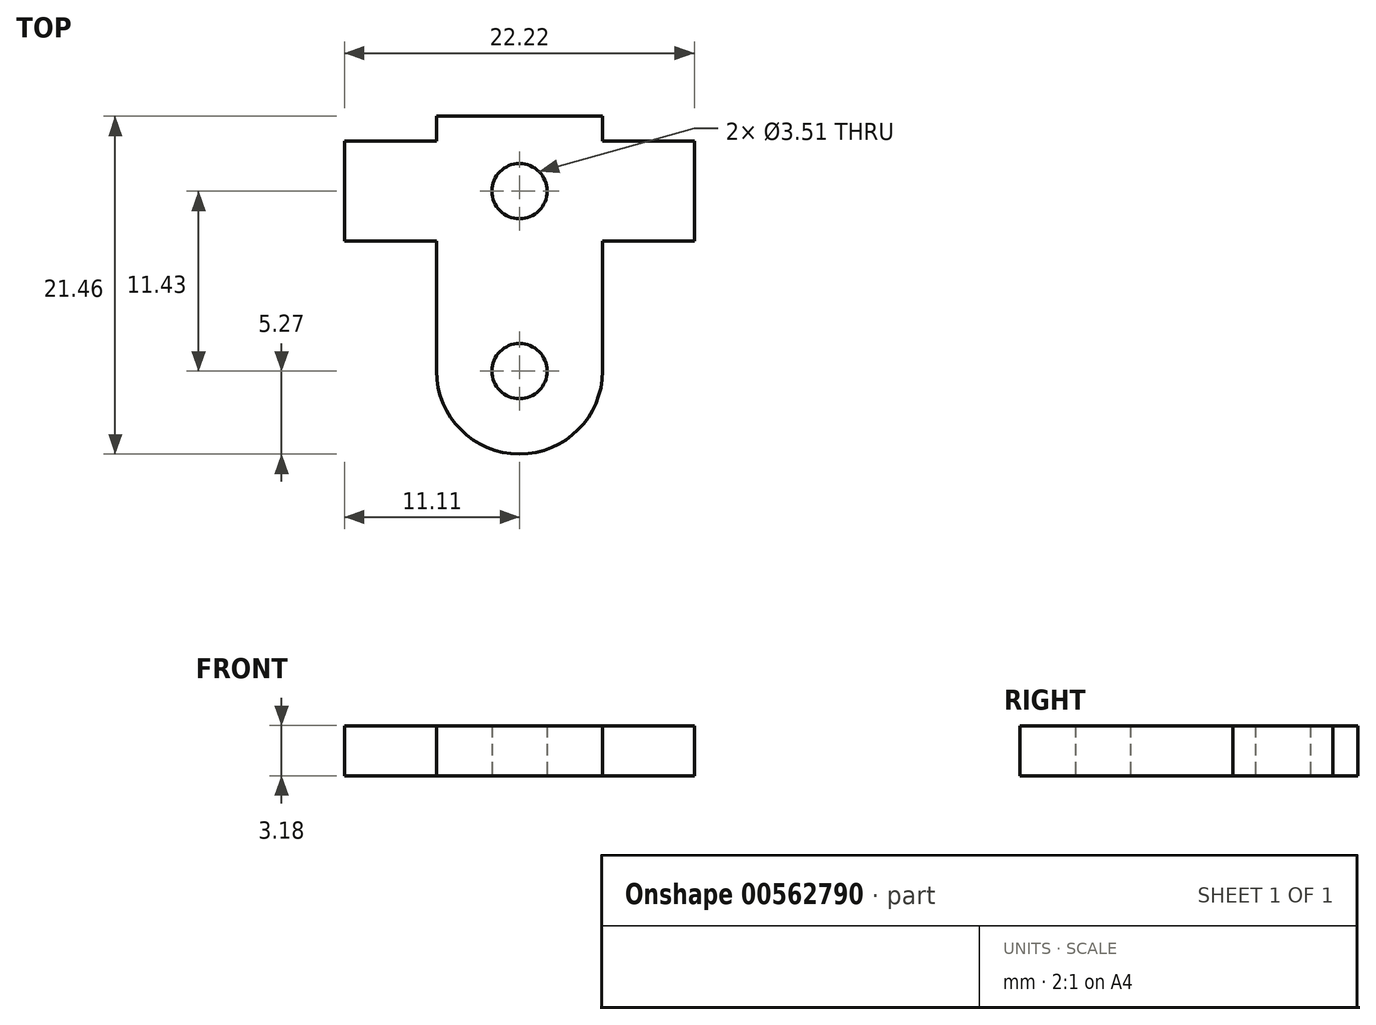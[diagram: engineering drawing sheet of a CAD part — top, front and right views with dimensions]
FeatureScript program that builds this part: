
annotation { "Feature Type Name" : "Feature", "Feature Type Description" : "" }
export const myFeature = defineFeature(function(context is Context, id is Id, definition is map)
    precondition{}
    {
        {
            var Q0;
            Q0=qCreatedBy(makeId("Top.planeOp"),FACE);
            var sketch = newSketch(context, id + "F0", { "sketchPlane" : qUnion([Q0])});
            skLineSegment(sketch, "E0.bottom", {"start": v(-11.11, 3.17) * mm, "end": v(-5.27, 3.17) * mm});
            skLineSegment(sketch, "E0.top", {"start": v(-11.11, -3.18) * mm, "end": v(-5.27, -3.18) * mm});
            skLineSegment(sketch, "E0.left", {"start": v(-11.11, 3.17) * mm, "end": v(-11.11, -3.18) * mm});
            skLineSegment(sketch, "E0.right", {"start": v(11.11, 3.17) * mm, "end": v(11.11, -3.18) * mm});
            skPoint(sketch, "E0.middle", {"position": v(0, 0) * mm});
            skLineSegment(sketch, "E1.top", {"start": v(-5.27, 4.76) * mm, "end": v(5.27, 4.76) * mm});
            skLineSegment(sketch, "E1.left", {"start": v(-5.27, 3.17) * mm, "end": v(-5.27, 4.76) * mm});
            skLineSegment(sketch, "E1.right", {"start": v(5.27, 3.17) * mm, "end": v(5.27, 4.76) * mm});
            skPoint(sketch, "E1.middle", {"position": v(0, 3.97) * mm});
            skLineSegment(sketch, "E2.trimOffspring", {"start": v(5.27, 3.17) * mm, "end": v(11.11, 3.17) * mm});
            skLineSegment(sketch, "E3.MirrorCS", {"start": v(5.27, -3.17) * mm, "end": v(5.27, -4.76) * mm});
            skLineSegment(sketch, "E4.MirrorCS", {"start": v(-5.27, -3.17) * mm, "end": v(-5.27, -4.76) * mm});
            skPoint(sketch, "E5.MirrorP", {"position": v(0, -3.97) * mm});
            skLineSegment(sketch, "E6.MirrorCS", {"start": v(-5.27, -4.76) * mm, "end": v(5.27, -4.76) * mm});
            skLineSegment(sketch, "E7.trimOffspring", {"start": v(5.27, -3.18) * mm, "end": v(11.11, -3.18) * mm});
            skSolve(sketch);
        }
        {
            var Q0;
            Q0 = qSketchRegion(id + "F0", true);
            extrude(context, id + "F1", {"entities" : qUnion([Q0]), "depth" : 3.17 * mm, "offsetDistance" : 25.4 * mm});
        }
        {
            var Q0;
            Q0=makeQuery(id+"F1.opExtrude","CAP_FACE",FACE,{"disambiguationData":[OSD([sQuery(id+"F0.wireOp",EDGE,"E0.bottom"),sQuery(id+"F0.wireOp",EDGE,"E0.top"),sQuery(id+"F0.wireOp",EDGE,"E0.left"),sQuery(id+"F0.wireOp",EDGE,"E0.right"),sQuery(id+"F0.wireOp",EDGE,"E1.top"),sQuery(id+"F0.wireOp",EDGE,"E1.left"),sQuery(id+"F0.wireOp",EDGE,"E1.right"),sQuery(id+"F0.wireOp",EDGE,"E2.trimOffspring"),sQuery(id+"F0.wireOp",EDGE,"E3.MirrorCS"),sQuery(id+"F0.wireOp",EDGE,"E4.MirrorCS"),sQuery(id+"F0.wireOp",EDGE,"E6.MirrorCS"),sQuery(id+"F0.wireOp",EDGE,"E7.trimOffspring")])],"isStart":true});
            var sketch = newSketch(context, id + "F2", { "sketchPlane" : qUnion([Q0])});
            skCircle(sketch, "E8", {"center": v(0, 11.43) * mm, "radius": 1.75 * mm});
            skArc(sketch, "E9", {"start": v(5.27, 11.43) * mm, "mid": v(0, 16.7) * mm, "end": v(-5.27, 11.43) * mm});
            skLineSegment(sketch, "E10", {"start": v(-5.27, 4.76) * mm, "end": v(-5.27, 11.43) * mm});
            skLineSegment(sketch, "E11", {"start": v(-5.27, 4.76) * mm, "end": v(5.27, 4.76) * mm});
            skLineSegment(sketch, "E12.MirrorCS", {"start": v(5.27, 4.76) * mm, "end": v(5.27, 11.43) * mm});
            skSolve(sketch);
        }
        {
            var Q0;
            Q0 = qSketchRegion(id + "F2", true);
            var Q1;
            Q1=makeQuery(id+"F1.opExtrude","CAP_FACE",FACE,{"disambiguationData":[OSD([sQuery(id+"F0.wireOp",EDGE,"E0.bottom"),sQuery(id+"F0.wireOp",EDGE,"E0.top"),sQuery(id+"F0.wireOp",EDGE,"E0.left"),sQuery(id+"F0.wireOp",EDGE,"E0.right"),sQuery(id+"F0.wireOp",EDGE,"E1.top"),sQuery(id+"F0.wireOp",EDGE,"E1.left"),sQuery(id+"F0.wireOp",EDGE,"E1.right"),sQuery(id+"F0.wireOp",EDGE,"E2.trimOffspring"),sQuery(id+"F0.wireOp",EDGE,"E3.MirrorCS"),sQuery(id+"F0.wireOp",EDGE,"E4.MirrorCS"),sQuery(id+"F0.wireOp",EDGE,"E6.MirrorCS"),sQuery(id+"F0.wireOp",EDGE,"E7.trimOffspring")])],"isStart":false});
            extrude(context, id + "F3", {"entities" : qUnion([Q0]), "operationType" : NewBodyOperationType.ADD, "endBound" : BoundingType.UP_TO_SURFACE, "oppositeDirection" : true, "depth" : 25.4 * mm, "endBoundEntityFace" : qUnion([Q1]), "offsetDistance" : 25.4 * mm});
        }
        {
            var Q0;
            Q0=makeQuery(id+"F3.boolean.opBoolean","MERGE",FACE,{"derivedFrom":[makeQuery(id+"F1.opExtrude","CAP_FACE",FACE,{"disambiguationData":[OSD([sQuery(id+"F0.wireOp",EDGE,"E0.bottom"),sQuery(id+"F0.wireOp",EDGE,"E0.top"),sQuery(id+"F0.wireOp",EDGE,"E0.left"),sQuery(id+"F0.wireOp",EDGE,"E0.right"),sQuery(id+"F0.wireOp",EDGE,"E1.top"),sQuery(id+"F0.wireOp",EDGE,"E1.left"),sQuery(id+"F0.wireOp",EDGE,"E1.right"),sQuery(id+"F0.wireOp",EDGE,"E2.trimOffspring"),sQuery(id+"F0.wireOp",EDGE,"E3.MirrorCS"),sQuery(id+"F0.wireOp",EDGE,"E4.MirrorCS"),sQuery(id+"F0.wireOp",EDGE,"E6.MirrorCS"),sQuery(id+"F0.wireOp",EDGE,"E7.trimOffspring")])],"isStart":true}),makeQuery(id+"F3.opExtrude","CAP_FACE",FACE,{"disambiguationData":[OSD([sQuery(id+"F2.wireOp",EDGE,"E8"),sQuery(id+"F2.wireOp",EDGE,"E9"),sQuery(id+"F2.wireOp",EDGE,"E10"),sQuery(id+"F2.wireOp",EDGE,"E11"),sQuery(id+"F2.wireOp",EDGE,"E12.MirrorCS")])],"isStart":true})]});
            var sketch = newSketch(context, id + "F4", { "sketchPlane" : qUnion([Q0])});
            skCircle(sketch, "E13", {"center": v(0, 0) * mm, "radius": 1.75 * mm});
            skSolve(sketch);
        }
        {
            var Q0;
            Q0 = qSketchRegion(id + "F4", true);
            extrude(context, id + "F5", {"entities" : qUnion([Q0]), "operationType" : NewBodyOperationType.REMOVE, "oppositeDirection" : true, "depth" : 25.4 * mm, "offsetDistance" : 25.4 * mm});
        }
    });
